# Revit family: Gira_126400
name_source: partatom
category: Electrical Fixtures
revit_build: Autodesk Revit 2017 (Build: 20160225_1515(x64)
units: mm (PartAtom-declared; Revit-internal decimal feet)

## family parameters
Cut with Voids When Loaded = No
Host = Face
Maintain Annotation Orientation = Yes
Part Type = Normal
Room Calculation Point = No
Round Connector Dimension = Use Diameter
Shared = No

## types (1)
- Info mod. door st. Gira TX_44 (WP FM)
    Available = No
    BIM (1) = https://media.stage.bim.site und Tasten.rfa?public/gira/36a6b08/TX44_Komplettgerät_Schalten und Tasten.rfa
    Category = Mounting accessories for door communication
    Data sheet (1) = https://katalog.gira.de
    Default Elevation = 1219 mm
    Description = Info mod.door st. TX_44,Info module for door station,,Program-neutral,Features:,- Installation in a conventional flush-mounted device box.,- Fits in the cover frames of the Gira TX_44 switch range.,- Modular design, allowing easy installation and expandability.,- Signal transmission and supply of the audio and video components via reverse-polarity-protected and short-circuit-proof 2-wire bus.,- Extension of the door station by an info module for display of the house number, name, or other information.,- Backlighting with LED technology, white light. Steady, clearly visible illumination is achieved using maintenance-free, energy-saving LED technology.,- Sprayed-water proof cover plate made of shock-resistant plastic.,- Inscription space can be exchanged without tools and without frame disassembly.,- Professional labelling is available from the Gira Inscription Service www.marking.gira.com or using the Gira inscription software.
    GTIN = 4010337264002
    HAN = 126400
    HeinzeBIM = https://bimportal.heinze.de
    Manufacturer = Gira
    Manufacturer URL = https://www.gira.de
    Material = Other
    Name = Info mod. door st. Gira TX_44 (WP FM)
    Suitable for = Outdoor station
    URL = http://katalog.gira.de

## geometry (parser evidence)
native form markers: Sweep x3
no freeform markers — native parametric forms only
